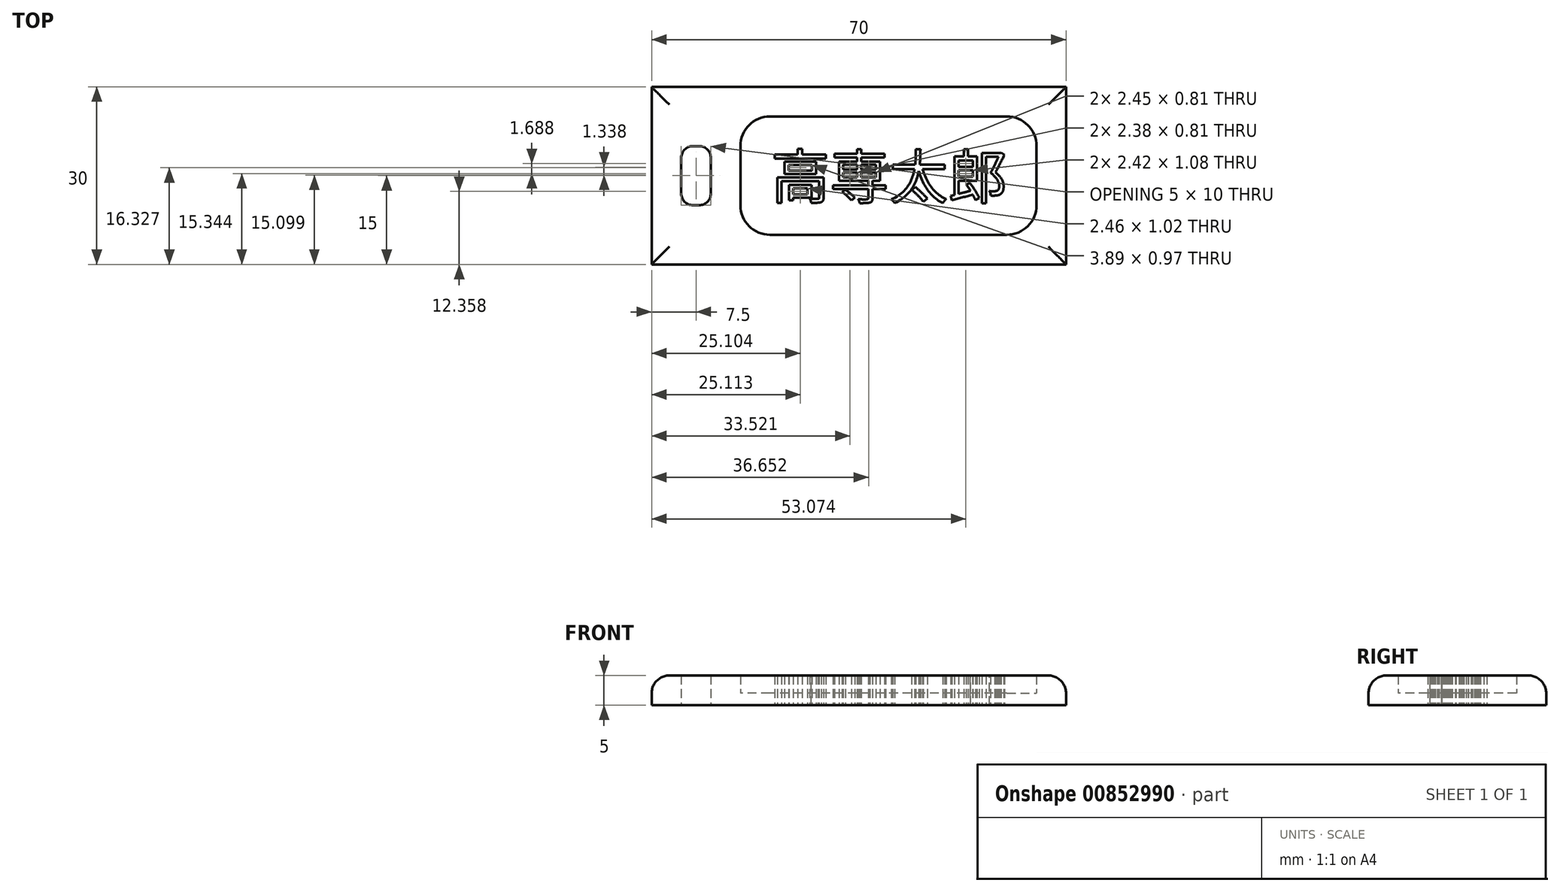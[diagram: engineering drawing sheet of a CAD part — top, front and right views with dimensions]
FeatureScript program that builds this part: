
annotation { "Feature Type Name" : "Feature", "Feature Type Description" : "" }
export const myFeature = defineFeature(function(context is Context, id is Id, definition is map)
    precondition{}
    {
        {
            var Q0;
            Q0=qCreatedBy(makeId("Top.planeOp"),FACE);
            var sketch = newSketch(context, id + "F0", { "sketchPlane" : qUnion([Q0])});
            skLineSegment(sketch, "E0.bottom", {"start": v(35, -15) * mm, "end": v(-35, -15) * mm});
            skLineSegment(sketch, "E0.top", {"start": v(35, 15) * mm, "end": v(-35, 15) * mm});
            skLineSegment(sketch, "E0.left", {"start": v(35, -15) * mm, "end": v(35, 15) * mm});
            skLineSegment(sketch, "E0.right", {"start": v(-35, -15) * mm, "end": v(-35, 15) * mm});
            skPoint(sketch, "E0.middle", {"position": v(0, 0) * mm});
            skSolve(sketch);
        }
        {
            var Q0;
            Q0=qCreatedBy(makeId("Top.planeOp"),FACE);
            var sketch = newSketch(context, id + "F1", { "sketchPlane" : qUnion([Q0])});
            skText(sketch, "E1", { "text": "高専太郎", "fontName": "NotoSansCJKjp-Regular.otf"});
            const initialGuessF1  = {"E1": [-0.01488, -0.00386, 1, 0, 0.00719]};
            skSetInitialGuess(sketch, initialGuessF1);
            skSolve(sketch);
        }
        {
            var Q0;
            Q0 = qSketchRegion(id + "F1", true);
            extrude(context, id + "F2", {"entities" : qUnion([Q0]), "depth" : 5 * mm, "offsetDistance" : 25 * mm});
        }
        {
            var Q0;
            Q0 = qSketchRegion(id + "F0", true);
            extrude(context, id + "F3", {"entities" : qUnion([Q0]), "depth" : 5 * mm, "offsetDistance" : 25 * mm});
        }
        {
            var Q0;
            Q0=qCreatedBy(makeId("Top.planeOp"),FACE);
            var sketch = newSketch(context, id + "F4", { "sketchPlane" : qUnion([Q0])});
            skLineSegment(sketch, "E2.bottom", {"start": v(-27, -5) * mm, "end": v(-28, -5) * mm});
            skLineSegment(sketch, "E2.top", {"start": v(-27, 5) * mm, "end": v(-28, 5) * mm});
            skLineSegment(sketch, "E2.left", {"start": v(-25, -3) * mm, "end": v(-25, 3) * mm});
            skLineSegment(sketch, "E2.right", {"start": v(-30, -3) * mm, "end": v(-30, 3) * mm});
            skPoint(sketch, "E2.middle", {"position": v(-27.5, 0) * mm});
            skPoint(sketch, "E3.visualSharp", {"position": v(-30, 5) * mm});
            skArc(sketch, "E3.filletArc", {"start": v(-28, 5) * mm, "mid": v(-29.41, 4.41) * mm, "end": v(-30, 3) * mm});
            skPoint(sketch, "E4.visualSharp", {"position": v(-25, 5) * mm});
            skArc(sketch, "E4.filletArc", {"start": v(-25, 3) * mm, "mid": v(-25.59, 4.41) * mm, "end": v(-27, 5) * mm});
            skPoint(sketch, "E5.visualSharp", {"position": v(-30, -5) * mm});
            skArc(sketch, "E5.filletArc", {"start": v(-30, -3) * mm, "mid": v(-29.41, -4.41) * mm, "end": v(-28, -5) * mm});
            skPoint(sketch, "E6.visualSharp", {"position": v(-25, -5) * mm});
            skArc(sketch, "E6.filletArc", {"start": v(-27, -5) * mm, "mid": v(-25.59, -4.41) * mm, "end": v(-25, -3) * mm});
            skSolve(sketch);
        }
        {
            var Q0;
            Q0 = qSketchRegion(id + "F4", true);
            extrude(context, id + "F5", {"entities" : qUnion([Q0]), "depth" : 6 * mm, "offsetDistance" : 25 * mm});
        }
        {
            var Q0;
            Q0=qCreatedBy(makeId("Top.planeOp"),FACE);
            var sketch = newSketch(context, id + "F6", { "sketchPlane" : qUnion([Q0])});
            skLineSegment(sketch, "E7.bottom", {"start": v(25, 10) * mm, "end": v(-15, 10) * mm});
            skLineSegment(sketch, "E7.top", {"start": v(25, -10) * mm, "end": v(-15, -10) * mm});
            skLineSegment(sketch, "E7.left", {"start": v(30, 5) * mm, "end": v(30, -5) * mm});
            skLineSegment(sketch, "E7.right", {"start": v(-20, 5) * mm, "end": v(-20, -5) * mm});
            skPoint(sketch, "E7.middle", {"position": v(5, 0) * mm});
            skPoint(sketch, "E8.visualSharp", {"position": v(-20, 10) * mm});
            skArc(sketch, "E8.filletArc", {"start": v(-15, 10) * mm, "mid": v(-18.54, 8.54) * mm, "end": v(-20, 5) * mm});
            skPoint(sketch, "E9.visualSharp", {"position": v(-20, -10) * mm});
            skArc(sketch, "E9.filletArc", {"start": v(-20, -5) * mm, "mid": v(-18.54, -8.54) * mm, "end": v(-15, -10) * mm});
            skPoint(sketch, "E10.visualSharp", {"position": v(30, 10) * mm});
            skArc(sketch, "E10.filletArc", {"start": v(30, 5) * mm, "mid": v(28.54, 8.54) * mm, "end": v(25, 10) * mm});
            skPoint(sketch, "E11.visualSharp", {"position": v(30, -10) * mm});
            skArc(sketch, "E11.filletArc", {"start": v(25, -10) * mm, "mid": v(28.54, -8.54) * mm, "end": v(30, -5) * mm});
            skSolve(sketch);
        }
        {
            var Q0;
            Q0 = qSketchRegion(id + "F6", true);
            extrude(context, id + "F7", {"entities" : qUnion([Q0]), "depth" : 6 * mm, "offsetDistance" : 25 * mm});
        }
        {
            var Q0;
            Q0=makeQuery(id+"F7.opExtrude","SWEPT_BODY",BODY,{"disambiguationData":[OSD([sQuery(id+"F6.wireOp",EDGE,"E7.bottom"),sQuery(id+"F6.wireOp",EDGE,"E7.top"),sQuery(id+"F6.wireOp",EDGE,"E7.left"),sQuery(id+"F6.wireOp",EDGE,"E7.right")])]});
            transform(context, id + "F8", {"entities" : qUnion([Q0]), "transformType" : TransformType.TRANSLATION_3D, "dx" : 0 * mm, "dy" : 0 * mm, "dz" : 2 * mm, "makeCopy" : false});
        }
        {
            var Q0;
            Q0=makeQuery(id+"F7.opExtrude","SWEPT_BODY",BODY,{"disambiguationData":[OSD([sQuery(id+"F6.wireOp",EDGE,"E7.bottom"),sQuery(id+"F6.wireOp",EDGE,"E7.top"),sQuery(id+"F6.wireOp",EDGE,"E7.left"),sQuery(id+"F6.wireOp",EDGE,"E7.right")])]});
            var Q1;
            Q1=makeQuery(id+"F3.opExtrude","SWEPT_BODY",BODY,{"disambiguationData":[OSD([sQuery(id+"F0.wireOp",EDGE,"E0.bottom"),sQuery(id+"F0.wireOp",EDGE,"E0.top"),sQuery(id+"F0.wireOp",EDGE,"E0.left"),sQuery(id+"F0.wireOp",EDGE,"E0.right")])]});
            booleanBodies(context, id + "F9", {"operationType" : BooleanOperationType.SUBTRACTION, "tools" : qUnion([Q0]), "targets" : qUnion([Q1])});
        }
        {
            var Q0;
            Q0=makeQuery(id+"F5.opExtrude","SWEPT_BODY",BODY,{"disambiguationData":[OSD([sQuery(id+"F4.wireOp",EDGE,"E2.bottom"),sQuery(id+"F4.wireOp",EDGE,"E2.top"),sQuery(id+"F4.wireOp",EDGE,"E2.left"),sQuery(id+"F4.wireOp",EDGE,"E2.right"),sQuery(id+"F4.wireOp",EDGE,"E3.filletArc"),sQuery(id+"F4.wireOp",EDGE,"E4.filletArc"),sQuery(id+"F4.wireOp",EDGE,"E5.filletArc"),sQuery(id+"F4.wireOp",EDGE,"E6.filletArc")])]});
            var Q1;
            Q1=makeQuery(id+"F3.opExtrude","SWEPT_BODY",BODY,{"disambiguationData":[OSD([sQuery(id+"F0.wireOp",EDGE,"E0.bottom"),sQuery(id+"F0.wireOp",EDGE,"E0.top"),sQuery(id+"F0.wireOp",EDGE,"E0.left"),sQuery(id+"F0.wireOp",EDGE,"E0.right")])]});
            booleanBodies(context, id + "F10", {"operationType" : BooleanOperationType.SUBTRACTION, "tools" : qUnion([Q0]), "targets" : qUnion([Q1])});
        }
        {
            var Q0;
            Q0=makeQuery(id+"F3.opExtrude","CAP_EDGE",EDGE,{"disambiguationData":[OSD([sQuery(id+"F0.wireOp",EDGE,"E0.right")])],"isStart":false});
            var Q1;
            Q1=makeQuery(id+"F3.opExtrude","CAP_EDGE",EDGE,{"disambiguationData":[OSD([sQuery(id+"F0.wireOp",EDGE,"E0.left")])],"isStart":false});
            var Q2;
            Q2=makeQuery(id+"F3.opExtrude","CAP_EDGE",EDGE,{"disambiguationData":[OSD([sQuery(id+"F0.wireOp",EDGE,"E0.top")])],"isStart":false});
            var Q3;
            Q3=makeQuery(id+"F3.opExtrude","CAP_EDGE",EDGE,{"disambiguationData":[OSD([sQuery(id+"F0.wireOp",EDGE,"E0.bottom")])],"isStart":false});
            fillet(context, id + "F11", {"entities" : qUnion([Q0, Q1, Q2, Q3]), "radius" : 3 * mm, "tangentPropagation" : true, "allowEdgeOverflow" : false});
        }
    });
